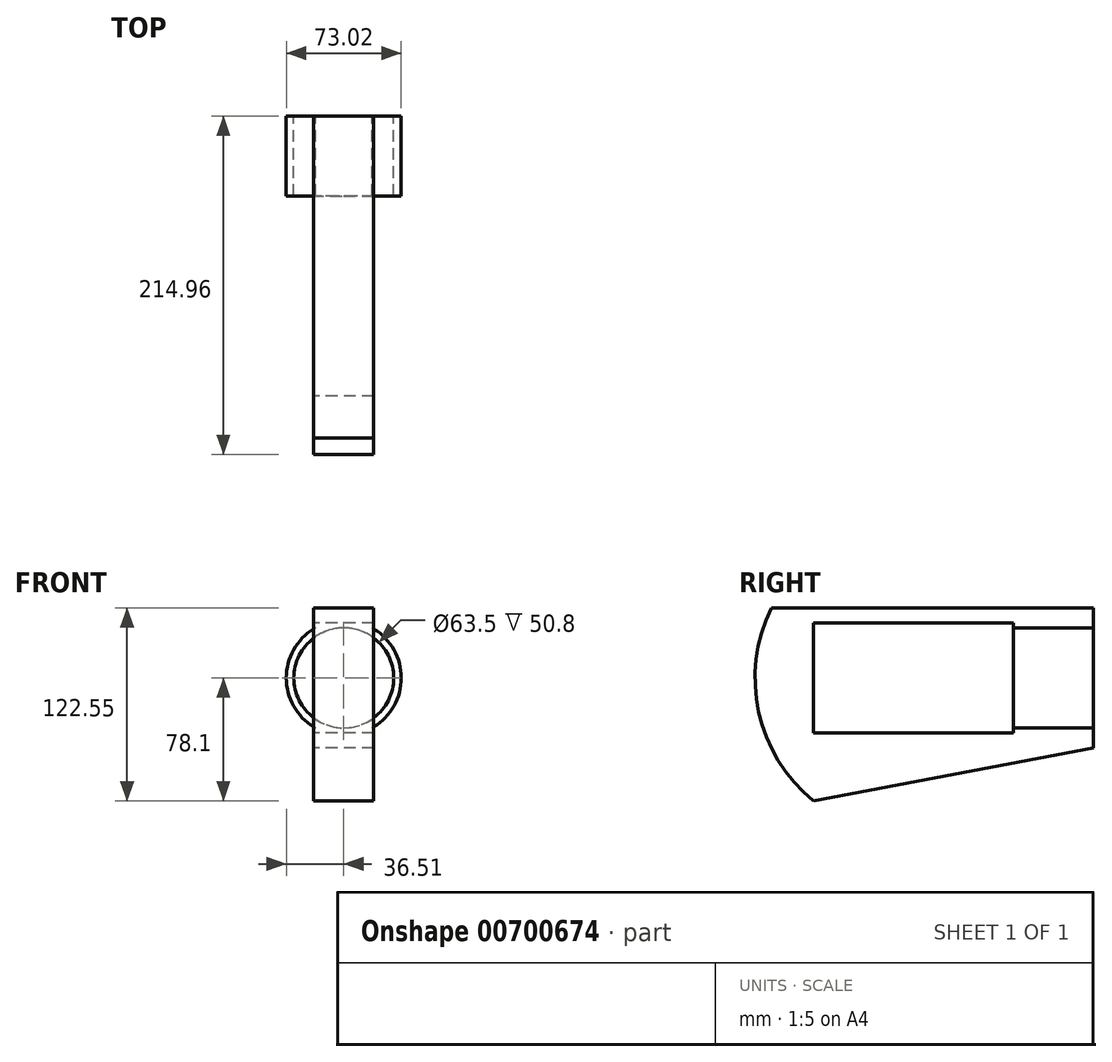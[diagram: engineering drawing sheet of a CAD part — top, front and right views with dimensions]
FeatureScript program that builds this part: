
annotation { "Feature Type Name" : "Feature", "Feature Type Description" : "" }
export const myFeature = defineFeature(function(context is Context, id is Id, definition is map)
    precondition{}
    {
        {
            var Q0;
            Q0=qCreatedBy(makeId("Right.planeOp"),FACE);
            var sketch = newSketch(context, id + "F0", { "sketchPlane" : qUnion([Q0])});
            skLineSegment(sketch, "E0", {"start": v(0, 0) * mm, "end": v(50.8, 0) * mm});
            skLineSegment(sketch, "E1", {"start": v(50.8, 0) * mm, "end": v(50.8, -12.7) * mm});
            skLineSegment(sketch, "E2", {"start": v(0, 0) * mm, "end": v(0, -3.18) * mm});
            skLineSegment(sketch, "E3", {"start": v(0, -3.18) * mm, "end": v(-127, -3.18) * mm});
            skLineSegment(sketch, "E4", {"start": v(-127, -3.18) * mm, "end": v(-127, 66.68) * mm});
            skLineSegment(sketch, "E5", {"start": v(-127, 66.68) * mm, "end": v(0, 66.68) * mm});
            skLineSegment(sketch, "E6", {"start": v(0, 66.68) * mm, "end": v(0, 63.5) * mm});
            skLineSegment(sketch, "E7", {"start": v(0, 63.5) * mm, "end": v(50.8, 63.5) * mm});
            skArc(sketch, "E8", {"start": v(-127, 109.85) * mm, "mid": v(-164.16, 31.75) * mm, "end": v(-127, -46.36) * mm});
            skLineSegment(sketch, "E9", {"start": v(50.8, 63.5) * mm, "end": v(50.8, 76.2) * mm});
            skLineSegment(sketch, "E10", {"start": v(-127, -46.36) * mm, "end": v(50.8, -12.7) * mm});
            skLineSegment(sketch, "E11", {"start": v(50.8, 76.2) * mm, "end": v(-127, 109.85) * mm});
            skSolve(sketch);
        }
        {
            var Q0;
            Q0 = qSketchRegion(id + "F0", true);
            extrude(context, id + "F1", {"entities" : qUnion([Q0]), "depth" : 38.1 * mm, "offsetDistance" : 25.4 * mm});
        }
        {
            var Q0;
            Q0=makeQuery(id+"F1.opExtrude","SWEPT_FACE",FACE,{"disambiguationData":[OSD([sQuery(id+"F0.wireOp",EDGE,"E9")])]});
            var sketch = newSketch(context, id + "F2", { "sketchPlane" : qUnion([Q0])});
            skCircle(sketch, "E12", {"center": v(-19.05, 31.75) * mm, "radius": 31.75 * mm});
            skCircle(sketch, "E13", {"center": v(-19.05, 31.75) * mm, "radius": 36.51 * mm});
            skSolve(sketch);
        }
        {
            var Q0;
            Q0 = qSketchRegion(id + "F2", true);
            extrude(context, id + "F3", {"entities" : qUnion([Q0]), "operationType" : NewBodyOperationType.ADD, "oppositeDirection" : true, "depth" : 50.8 * mm, "offsetDistance" : 25.4 * mm});
        }
        {
            var Q0;
            Q0=makeQuery(id+"F1.opExtrude","CAP_FACE",FACE,{"disambiguationData":[OSD([sQuery(id+"F0.wireOp",EDGE,"E0"),sQuery(id+"F0.wireOp",EDGE,"E1"),sQuery(id+"F0.wireOp",EDGE,"E2"),sQuery(id+"F0.wireOp",EDGE,"E3"),sQuery(id+"F0.wireOp",EDGE,"E4"),sQuery(id+"F0.wireOp",EDGE,"E5"),sQuery(id+"F0.wireOp",EDGE,"E6"),sQuery(id+"F0.wireOp",EDGE,"E7"),sQuery(id+"F0.wireOp",EDGE,"E8"),sQuery(id+"F0.wireOp",EDGE,"E9"),sQuery(id+"F0.wireOp",EDGE,"E10"),sQuery(id+"F0.wireOp",EDGE,"E11")])],"isStart":false});
            var sketch = newSketch(context, id + "F4", { "sketchPlane" : qUnion([Q0])});
            skLineSegment(sketch, "E14", {"start": v(50.8, 76.2) * mm, "end": v(-153.82, 76.2) * mm});
            skArc(sketch, "E15.0", {"start": v(-127, 109.85) * mm, "mid": v(-142.23, 94.48) * mm, "end": v(-153.82, 76.2) * mm});
            skLineSegment(sketch, "E16.0", {"start": v(50.8, 76.2) * mm, "end": v(-127, 109.85) * mm});
            skPoint(sketch, "E17.orphan", {"position": v(-127, -46.36) * mm});
            skSolve(sketch);
        }
        {
            var Q0;
            Q0 = qSketchRegion(id + "F4", true);
            extrude(context, id + "F5", {"entities" : qUnion([Q0]), "operationType" : NewBodyOperationType.REMOVE, "oppositeDirection" : true, "depth" : 127 * mm, "offsetDistance" : 25.4 * mm});
        }
    });
